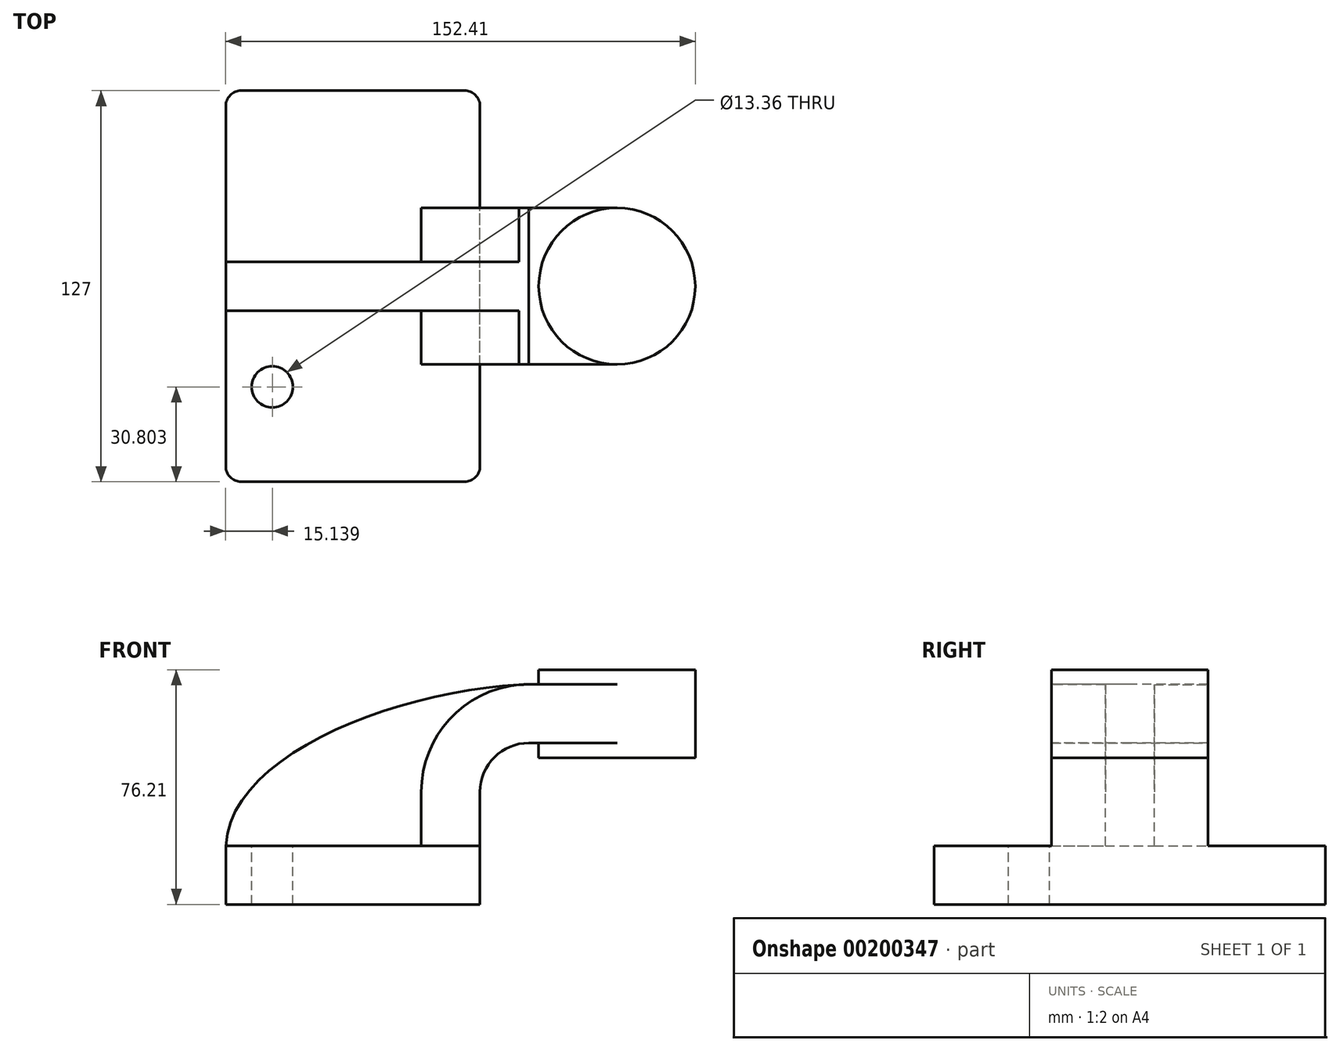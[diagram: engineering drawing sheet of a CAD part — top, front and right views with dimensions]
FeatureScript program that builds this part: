
annotation { "Feature Type Name" : "Feature", "Feature Type Description" : "" }
export const myFeature = defineFeature(function(context is Context, id is Id, definition is map)
    precondition{}
    {
        {
            var Q0;
            Q0=qCreatedBy(makeId("Front.planeOp"),FACE);
            var sketch = newSketch(context, id + "F0", { "sketchPlane" : qUnion([Q0])});
            skLineSegment(sketch, "E0.rect.bottom", {"start": v(-41.28, 9.52) * mm, "end": v(41.28, 9.52) * mm});
            skLineSegment(sketch, "E0.rect.top", {"start": v(-41.28, -9.52) * mm, "end": v(41.28, -9.52) * mm});
            skLineSegment(sketch, "E0.rect.left", {"start": v(-41.28, 9.52) * mm, "end": v(-41.28, -9.52) * mm});
            skLineSegment(sketch, "E0.rect.right", {"start": v(41.28, 9.52) * mm, "end": v(41.28, -9.52) * mm});
            skPoint(sketch, "E0.rect.middle", {"position": v(0, 0) * mm});
            skLineSegment(sketch, "E1", {"start": v(41.28, 9.52) * mm, "end": v(41.28, 27) * mm});
            skArc(sketch, "E2", {"start": v(41.28, 27) * mm, "mid": v(45.92, 38.23) * mm, "end": v(57.15, 42.88) * mm});
            skLineSegment(sketch, "E3", {"start": v(57.15, 42.88) * mm, "end": v(85.72, 42.88) * mm});
            skLineSegment(sketch, "E4.rect.bottom", {"start": v(60.32, 38.1) * mm, "end": v(111.12, 38.1) * mm});
            skLineSegment(sketch, "E4.rect.top", {"start": v(60.32, 66.68) * mm, "end": v(111.12, 66.68) * mm});
            skLineSegment(sketch, "E4.rect.left", {"start": v(60.32, 38.1) * mm, "end": v(60.32, 66.68) * mm});
            skLineSegment(sketch, "E4.rect.right", {"start": v(111.13, 38.1) * mm, "end": v(111.12, 66.68) * mm});
            skPoint(sketch, "E4.rect.middle", {"position": v(85.72, 52.39) * mm});
            skLineSegment(sketch, "E5.0", {"start": v(57.15, 61.93) * mm, "end": v(85.72, 61.93) * mm});
            skArc(sketch, "E5.1", {"start": v(22.23, 27) * mm, "mid": v(32.45, 51.7) * mm, "end": v(57.15, 61.93) * mm});
            skLineSegment(sketch, "E5.2", {"start": v(22.23, 9.52) * mm, "end": v(22.23, 27) * mm});
            skLineSegment(sketch, "E6", {"start": v(85.72, 38.1) * mm, "end": v(85.72, 66.68) * mm});
            skFitSpline(sketch, "E7", {"points": [v(-41.28, 9.53) * mm, v(57.15, 61.93) * mm], "startDerivative": vector(5.2, 92.34) * mm, "endDerivative": vector(120.92, 4.22) * mm});
            skSolve(sketch);
        }
        {
            var Q0;
            Q0=makeQuery(id+"F0.imprint","IMPRINT",FACE,{"disambiguationData":[TD([[makeQuery(id+"F0.imprint","IMPRINT",EDGE,{"derivedFrom":sQuery(id+"F0.wireOp",EDGE,"E0.rect.top")}),1.0]])]});
            extrude(context, id + "F1", {"entities" : qUnion([Q0]), "endBound" : BoundingType.SYMMETRIC, "depth" : 127 * mm});
        }
        {
            var Q0;
            {var subQ9=sQuery(id+"F0.wireOp",EDGE,"E1");Q0=makeQuery(id+"F0.imprint","IMPRINT",FACE,{"disambiguationData":[TD([[makeQuery(id+"F0.imprint","IMPRINT",EDGE,{"derivedFrom":subQ9}),1.0]])]});}
            var Q1;
            {var subQ0=sQuery(id+"F0.wireOp",EDGE,"E6");var subQ1=sQuery(id+"F0.wireOp",EDGE,"E3");var subQ2=makeQuery(id+"F0.imprint","INTERSECT",VERTEX,{"derivedFrom":[subQ1,subQ0]});Q1=makeQuery(id+"F0.imprint","IMPRINT",FACE,{"disambiguationData":[TD([[makeQuery(id+"F0.imprint","IMPRINT",EDGE,{"disambiguationData":[TD([[subQ2,1.0]])],"derivedFrom":subQ1}),1.0]])]});}
            extrude(context, id + "F2", {"entities" : qUnion([Q0, Q1]), "operationType" : NewBodyOperationType.ADD, "endBound" : BoundingType.SYMMETRIC, "depth" : 50.8 * mm});
        }
        {
            var Q0;
            {var subQ3=sQuery(id+"F0.wireOp",EDGE,"E5.2");Q0=makeQuery(id+"F0.imprint","IMPRINT",FACE,{"disambiguationData":[TD([[makeQuery(id+"F0.imprint","IMPRINT",EDGE,{"derivedFrom":subQ3}),1.0]])]});}
            extrude(context, id + "F3", {"entities" : qUnion([Q0]), "operationType" : NewBodyOperationType.ADD, "endBound" : BoundingType.SYMMETRIC, "depth" : 15.88 * mm});
        }
        {
            var Q0;
            {var subQ5=sQuery(id+"F0.wireOp",EDGE,"E4.rect.right");Q0=makeQuery(id+"F0.imprint","IMPRINT",FACE,{"disambiguationData":[TD([[makeQuery(id+"F0.imprint","IMPRINT",EDGE,{"derivedFrom":subQ5}),1.0]])]});}
            var Q1;
            Q1=sQuery(id+"F0.wireOp",EDGE,"E6");
            revolve(context, id + "F4", {"operationType" : NewBodyOperationType.ADD, "entities" : qUnion([Q0]), "axis" : qUnion([Q1]), "revolveType" : RevolveType.FULL});
        }
        {
            var Q0;
            Q0=makeQuery(id+"F1.opExtrude","CAP_EDGE",EDGE,{"disambiguationData":[OSD([sQuery(id+"F0.wireOp",EDGE,"E0.rect.right")])],"isStart":false});
            var Q1;
            Q1=makeQuery(id+"F1.opExtrude","CAP_EDGE",EDGE,{"disambiguationData":[OSD([sQuery(id+"F0.wireOp",EDGE,"E0.rect.left")])],"isStart":false});
            var Q2;
            Q2=makeQuery(id+"F1.opExtrude","CAP_EDGE",EDGE,{"disambiguationData":[OSD([sQuery(id+"F0.wireOp",EDGE,"E0.rect.right")])],"isStart":true});
            var Q3;
            Q3=makeQuery(id+"F1.opExtrude","CAP_EDGE",EDGE,{"disambiguationData":[OSD([sQuery(id+"F0.wireOp",EDGE,"E0.rect.left")])],"isStart":true});
            fillet(context, id + "F5", {"entities" : qUnion([Q0, Q1, Q2, Q3]), "radius" : 5.08 * mm, "tangentPropagation" : true, "allowEdgeOverflow" : false});
        }
        {
            var Q0;
            {var subQ4=sQuery(id+"F0.wireOp",EDGE,"E0.rect.bottom");var subQ5=sQuery(id+"F0.wireOp",EDGE,"E0.rect.right");var subQ6=sQuery(id+"F0.wireOp",EDGE,"E0.rect.left");Q0=makeQuery(id+"F3.boolean.opBoolean","SPLIT",FACE,{"disambiguationData":[TD([makeQuery(id+"F1.opExtrude","CAP_FACE",FACE,{"disambiguationData":[OSD([subQ4,sQuery(id+"F0.wireOp",EDGE,"E0.rect.top"),subQ6,subQ5])],"isStart":false})])],"derivedFrom":makeQuery(id+"F1.opExtrude","SWEPT_FACE",FACE,{"disambiguationData":[OSD([subQ4])]})});}
            var sketch = newSketch(context, id + "F6", { "sketchPlane" : qUnion([Q0])});
            skCircle(sketch, "E8", {"center": v(-26.14, -32.7) * mm, "radius": 6.68 * mm});
            skSolve(sketch);
        }
        {
            var Q0;
            Q0=makeQuery(id+"F6.imprint","IMPRINT",FACE,{"disambiguationData":[TD([[makeQuery(id+"F6.imprint","IMPRINT",EDGE,{"derivedFrom":sQuery(id+"F6.wireOp",EDGE,"E8")}),1.0]])]});
            extrude(context, id + "F7", {"entities" : qUnion([Q0]), "operationType" : NewBodyOperationType.REMOVE, "oppositeDirection" : true, "depth" : 25.4 * mm});
        }
    });
